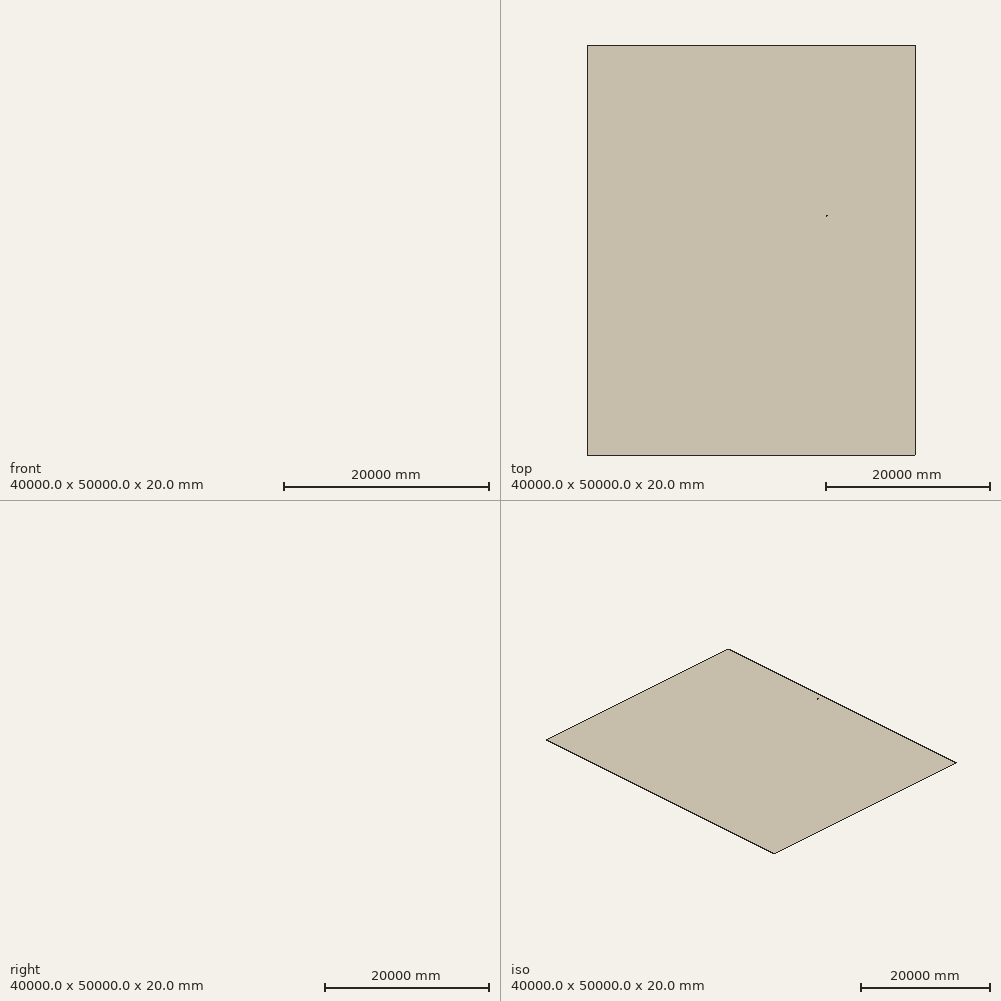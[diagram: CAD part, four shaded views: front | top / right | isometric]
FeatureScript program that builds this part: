
annotation { "Feature Type Name" : "Feature", "Feature Type Description" : "" }
export const myFeature = defineFeature(function(context is Context, id is Id, definition is map)
    precondition{}
    {
        {
            var Q0;
            Q0=qCreatedBy(makeId("Top.planeOp"),FACE);
            var sketch = newSketch(context, id + "F0", { "sketchPlane" : qUnion([Q0])});
            skLineSegment(sketch, "E0.bottom", {"start": v(-40123.28, 49756.41) * mm, "end": v(-123.28, 49756.41) * mm});
            skLineSegment(sketch, "E0.top", {"start": v(-40123.28, -243.59) * mm, "end": v(-123.28, -243.59) * mm});
            skLineSegment(sketch, "E0.left", {"start": v(-40123.28, 49756.41) * mm, "end": v(-40123.28, -243.59) * mm});
            skLineSegment(sketch, "E0.right", {"start": v(-123.28, 49756.41) * mm, "end": v(-123.28, -243.59) * mm});
            skCircle(sketch, "E1", {"center": v(-39723.28, 156.41) * mm, "radius": 20 * mm});
            skCircle(sketch, "E2.0.1.0", {"center": v(-39723.28, 9756.41) * mm, "radius": 20 * mm});
            skCircle(sketch, "E2.0.2.0", {"center": v(-39723.28, 19356.41) * mm, "radius": 20 * mm});
            skCircle(sketch, "E2.0.3.0", {"center": v(-39723.28, 28956.41) * mm, "radius": 20 * mm});
            skCircle(sketch, "E2.0.4.0", {"center": v(-39723.28, 38556.41) * mm, "radius": 20 * mm});
            skCircle(sketch, "E2.1.0.0", {"center": v(-30123.28, 156.41) * mm, "radius": 20 * mm});
            skCircle(sketch, "E2.1.1.0", {"center": v(-30123.28, 9756.41) * mm, "radius": 20 * mm});
            skCircle(sketch, "E2.1.2.0", {"center": v(-30123.28, 19356.41) * mm, "radius": 20 * mm});
            skCircle(sketch, "E2.1.3.0", {"center": v(-30123.28, 28956.41) * mm, "radius": 20 * mm});
            skCircle(sketch, "E2.1.4.0", {"center": v(-30123.28, 38556.41) * mm, "radius": 20 * mm});
            skCircle(sketch, "E2.2.0.0", {"center": v(-20523.28, 156.41) * mm, "radius": 20 * mm});
            skCircle(sketch, "E2.2.1.0", {"center": v(-20523.28, 9756.41) * mm, "radius": 20 * mm});
            skCircle(sketch, "E2.2.2.0", {"center": v(-20523.28, 19356.41) * mm, "radius": 20 * mm});
            skCircle(sketch, "E2.2.3.0", {"center": v(-20523.28, 28956.41) * mm, "radius": 20 * mm});
            skCircle(sketch, "E2.2.4.0", {"center": v(-20523.28, 38556.41) * mm, "radius": 20 * mm});
            skCircle(sketch, "E2.3.0.0", {"center": v(-10923.28, 156.41) * mm, "radius": 20 * mm});
            skCircle(sketch, "E2.3.1.0", {"center": v(-10923.28, 9756.41) * mm, "radius": 20 * mm});
            skCircle(sketch, "E2.3.2.0", {"center": v(-10923.28, 19356.41) * mm, "radius": 20 * mm});
            skCircle(sketch, "E2.3.3.0", {"center": v(-10923.28, 28956.41) * mm, "radius": 20 * mm});
            skCircle(sketch, "E2.3.4.0", {"center": v(-10923.28, 38556.41) * mm, "radius": 20 * mm});
            skCircle(sketch, "E2.4.0.0", {"center": v(-1323.28, 156.41) * mm, "radius": 20 * mm});
            skCircle(sketch, "E2.4.1.0", {"center": v(-1323.28, 9756.41) * mm, "radius": 20 * mm});
            skCircle(sketch, "E2.4.2.0", {"center": v(-1323.28, 19356.41) * mm, "radius": 20 * mm});
            skCircle(sketch, "E2.4.3.0", {"center": v(-1323.28, 28956.41) * mm, "radius": 20 * mm});
            skCircle(sketch, "E2.4.4.0", {"center": v(-1323.28, 38556.41) * mm, "radius": 20 * mm});
            skLineSegment(sketch, "E2.direction1", {"start": v(-39723.28, 156.41) * mm, "end": v(-30123.28, 156.41) * mm, "construction": true});
            skLineSegment(sketch, "E2.direction2", {"start": v(-39723.28, 156.41) * mm, "end": v(-39723.28, 9756.41) * mm, "construction": true});
            skCircle(sketch, "E3.0.0.5", {"center": v(-39723.28, 48156.41) * mm, "radius": 20 * mm});
            skCircle(sketch, "E3.0.1.5", {"center": v(-30123.28, 48156.41) * mm, "radius": 20 * mm});
            skCircle(sketch, "E3.0.2.5", {"center": v(-20523.28, 48156.41) * mm, "radius": 20 * mm});
            skCircle(sketch, "E3.0.3.5", {"center": v(-10923.28, 48156.41) * mm, "radius": 20 * mm});
            skCircle(sketch, "E3.0.4.5", {"center": v(-1323.28, 48156.41) * mm, "radius": 20 * mm});
            skSolve(sketch);
        }
        {
            var Q0;
            Q0=makeQuery(id+"F0.imprint","IMPRINT",FACE,{"disambiguationData":[TD([[makeQuery(id+"F0.imprint","IMPRINT",EDGE,{"derivedFrom":sQuery(id+"F0.wireOp",EDGE,"E0.bottom")}),-1.0]])]});
            extrude(context, id + "F1", {"entities" : qUnion([Q0]), "endBound" : BoundingType.SYMMETRIC, "depth" : 20 * mm, "offsetDistance" : 25 * mm});
        }
    });
